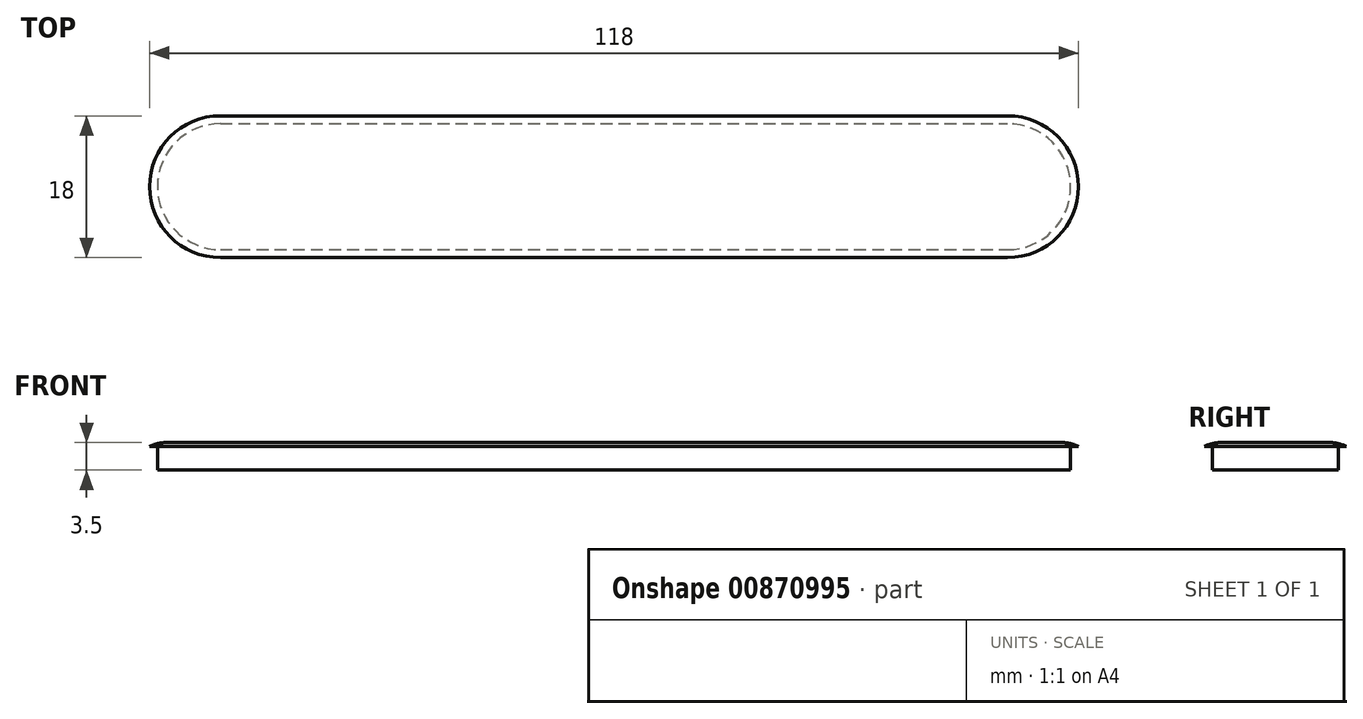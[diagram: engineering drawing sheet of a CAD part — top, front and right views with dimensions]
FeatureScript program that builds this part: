
annotation { "Feature Type Name" : "Feature", "Feature Type Description" : "" }
export const myFeature = defineFeature(function(context is Context, id is Id, definition is map)
    precondition{}
    {
        {
            var Q0;
            Q0=qCreatedBy(makeId("Top.planeOp"),FACE);
            var sketch = newSketch(context, id + "F0", { "sketchPlane" : qUnion([Q0])});
            skLineSegment(sketch, "E0.bottom", {"start": v(-28.2, 8) * mm, "end": v(71.8, 8) * mm});
            skLineSegment(sketch, "E0.top", {"start": v(-28.2, -8) * mm, "end": v(71.8, -8) * mm});
            skArc(sketch, "E1", {"start": v(-28.2, 8) * mm, "mid": v(-36.2, 0) * mm, "end": v(-28.2, -8) * mm});
            skArc(sketch, "E2", {"start": v(71.8, -8) * mm, "mid": v(79.8, 0) * mm, "end": v(71.8, 8) * mm});
            skSolve(sketch);
        }
        {
            var Q0;
            Q0=makeQuery(id+"F0.imprint","IMPRINT",FACE,{"disambiguationData":[TD([[makeQuery(id+"F0.imprint","IMPRINT",EDGE,{"derivedFrom":sQuery(id+"F0.wireOp",EDGE,"E0.bottom")}),-1.0]])]});
            extrude(context, id + "F1", {"entities" : qUnion([Q0]), "depth" : 3 * mm, "offsetDistance" : 25 * mm});
        }
        {
            var Q0;
            Q0=makeQuery(id+"F1.opExtrude","CAP_FACE",FACE,{"disambiguationData":[OSD([sQuery(id+"F0.wireOp",EDGE,"E0.bottom"),sQuery(id+"F0.wireOp",EDGE,"E0.top"),sQuery(id+"F0.wireOp",EDGE,"E1"),sQuery(id+"F0.wireOp",EDGE,"E2")])],"isStart":false});
            var sketch = newSketch(context, id + "F2", { "sketchPlane" : qUnion([Q0])});
            skLineSegment(sketch, "E3", {"start": v(-28.2, 9) * mm, "end": v(71.8, 9) * mm});
            skLineSegment(sketch, "E4", {"start": v(-28.2, -9) * mm, "end": v(71.8, -9) * mm});
            skArc(sketch, "E5", {"start": v(-28.2, 9) * mm, "mid": v(-37.2, 0) * mm, "end": v(-28.2, -9) * mm});
            skArc(sketch, "E6", {"start": v(71.8, -9) * mm, "mid": v(80.8, 0) * mm, "end": v(71.8, 9) * mm});
            skSolve(sketch);
        }
        {
            var Q0;
            Q0=makeQuery(id+"F2.imprint","IMPRINT",FACE,{"disambiguationData":[TD([[makeQuery(id+"F2.imprint","IMPRINT",EDGE,{"derivedFrom":sQuery(id+"F2.wireOp",EDGE,"E3")}),-1.0]])]});
            var Q1;
            Q1=makeQuery(id+"F2.imprint","IMPRINT",FACE,{"disambiguationData":[TD([[makeQuery(id+"F2.imprint","IMPRINT",EDGE,{"derivedFrom":makeQuery(id+"F1.opExtrude","CAP_EDGE",EDGE,{"disambiguationData":[OSD([sQuery(id+"F0.wireOp",EDGE,"E0.bottom")])],"isStart":false})}),-1.0]])]});
            extrude(context, id + "F3", {"entities" : qUnion([Q0, Q1]), "operationType" : NewBodyOperationType.ADD, "depth" : 0.5 * mm, "offsetDistance" : 25 * mm});
        }
        {
            var Q0;
            Q0=makeQuery(id+"F3.opExtrude","CAP_EDGE",EDGE,{"disambiguationData":[OSD([sQuery(id+"F2.wireOp",EDGE,"E5")])],"isStart":false});
            var Q1;
            Q1=makeQuery(id+"F3.opExtrude","CAP_EDGE",EDGE,{"disambiguationData":[OSD([sQuery(id+"F2.wireOp",EDGE,"E4")])],"isStart":false});
            var Q2;
            Q2=makeQuery(id+"F3.opExtrude","CAP_EDGE",EDGE,{"disambiguationData":[OSD([sQuery(id+"F2.wireOp",EDGE,"E3")])],"isStart":false});
            var Q3;
            Q3=makeQuery(id+"F3.opExtrude","CAP_EDGE",EDGE,{"disambiguationData":[OSD([sQuery(id+"F2.wireOp",EDGE,"E6")])],"isStart":false});
            fillet(context, id + "F4", {"entities" : qUnion([Q0, Q1, Q2, Q3]), "tangentPropagation" : true, "radius" : 5 * mm, "defaultsChanged" : false, "vertexSettings" : [], "allowEdgeOverflow" : false});
        }
    });
